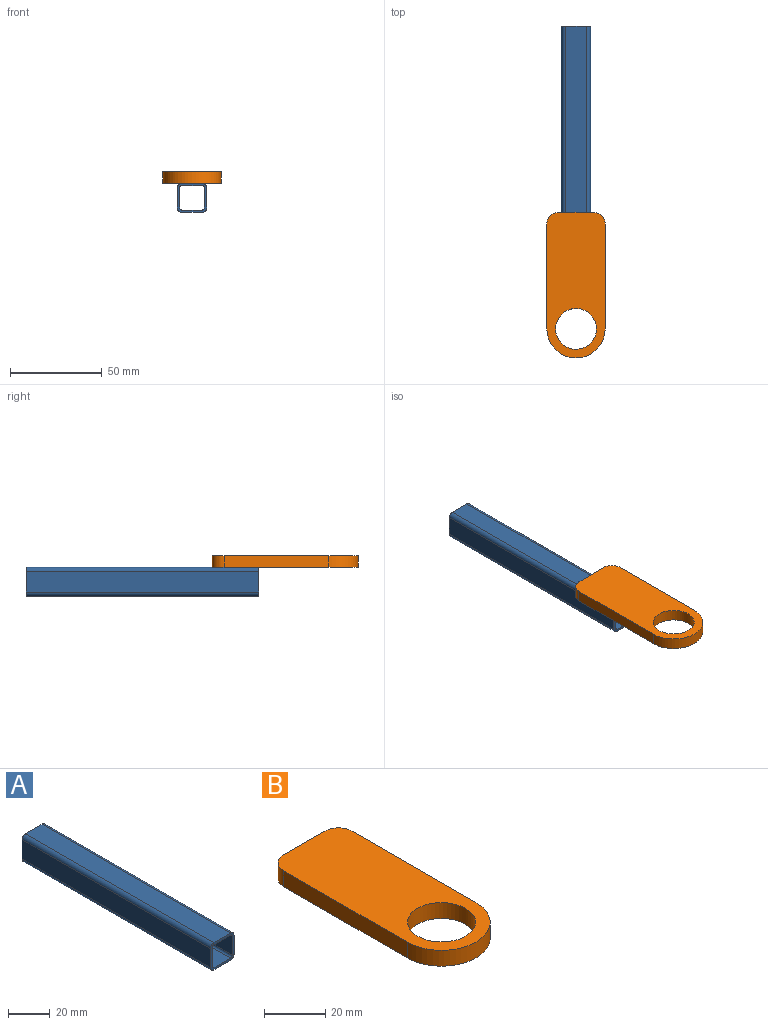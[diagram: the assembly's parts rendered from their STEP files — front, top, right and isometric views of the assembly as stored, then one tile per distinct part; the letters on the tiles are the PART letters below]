
ASSEMBLY  parts=2 mates=1
PART A: 18 faces, bbox 15.9x127x15.9 mm
  f0: plane 127x11.11mm, normal (1,0,0), area 1411.3mm2, adj f1,f15,f16,f17
  f1: cylinder r=2.38mm len=127mm, axis (0,1,0), area 475mm2, adj f0,f2,f16,f17
  f2: plane 127x11.11mm, normal (0,0,1), area 1411.3mm2, adj f1,f3,f16,f17
  f3: cylinder r=2.38mm len=127mm, axis (0,1,0), area 475mm2, adj f2,f4,f16,f17
  f4: plane 127x11.11mm, normal (-1,0,0), area 1411.3mm2, adj f3,f5,f16,f17
  f5: cylinder r=2.38mm len=127mm, axis (0,1,0), area 475mm2, adj f4,f6,f16,f17
  f6: plane 127x11.11mm, normal (0,0,-1), area 1411.3mm2, adj f5,f15,f16,f17
  f7: cylinder r=1.14mm len=127mm, axis (0,1,0), area 226.8mm2, adj f8,f14,f16,f17
  f8: plane 127x11.11mm, normal (0,0,-1), area 1411.3mm2, adj f7,f9,f16,f17
  f9: cylinder r=1.14mm len=127mm, axis (0,1,0), area 226.8mm2, adj f8,f10,f16,f17
  f10: plane 127x11.11mm, normal (-1,0,0), area 1411.3mm2, adj f9,f11,f16,f17
  f11: cylinder r=1.14mm len=127mm, axis (0,1,0), area 226.8mm2, adj f10,f12,f16,f17
  f12: plane 127x11.11mm, normal (0,0,1), area 1411.3mm2, adj f11,f13,f16,f17
  f13: cylinder r=1.14mm len=127mm, axis (0,1,0), area 226.8mm2, adj f12,f14,f16,f17
  f14: plane 127x11.11mm, normal (1,0,0), area 1411.3mm2, adj f7,f13,f16,f17
  f15: cylinder r=2.38mm len=127mm, axis (0,1,0), area 475mm2, adj f0,f6,f16,f17
  f16: plane 15.88x15.88mm, normal (0,-1,0), area 69.1mm2, adj f0,f1,f2,f3,f4,f5,f6,f7
  f17: plane 15.88x15.88mm, normal (0,1,0), area 69.1mm2, adj f0,f1,f2,f3,f4,f5,f6,f7
PART B: 9 faces, bbox 31.8x79.4x6.4 mm
  f0: cylinder r=6.35mm len=6.35mm, axis (0,0,-1), area 63.3mm2, adj f1,f6,f7,f8
  f1: plane 57.15x6.35mm, normal (-1,0,0), area 362.9mm2, adj f0,f2,f7,f8
  f2: cylinder r=15.88mm len=31.75mm, axis (0,0,-1), area 316.7mm2, adj f1,f3,f7,f8
  f3: plane 57.15x6.35mm, normal (1,0,0), area 362.9mm2, adj f2,f4,f7,f8
  f4: cylinder r=6.35mm len=6.35mm, axis (0,0,-1), area 63.3mm2, adj f3,f6,f7,f8
  f5: cylinder r=11.11mm len=22.23mm, axis (0,0,-1), area 443.4mm2, adj f7,f8
  f6: plane 19.05x6.35mm, normal (0,1,0), area 121mm2, adj f0,f4,f7,f8
  f7: plane 79.38x31.75mm, normal (0,0,1), area 2006.7mm2, adj f0,f1,f2,f3,f4,f5,f6
  f8: plane 79.38x31.75mm, normal (0,0,-1), area 2006.7mm2, adj f0,f1,f2,f3,f4,f5,f6
PLACE A at identity fixed
PLACE B t=(0,-133.35,7.94)mm
MATE fastened B.f8 <-> A.f2  axis (0,0,-1) through (0,-101.6,7.94)mm
